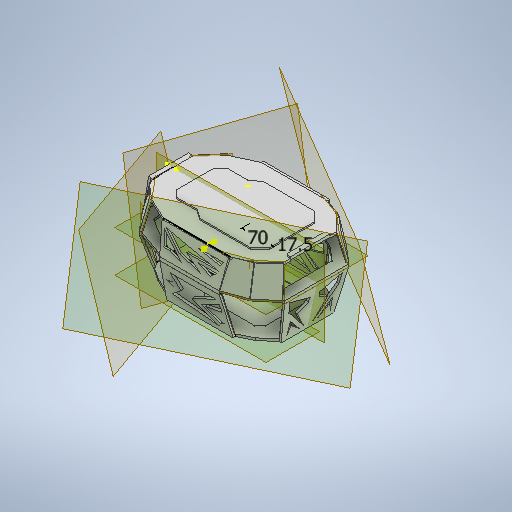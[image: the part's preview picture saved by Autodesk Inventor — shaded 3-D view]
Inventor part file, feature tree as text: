
AUTODESK INVENTOR PART (.ipt)
format: ipt  version: 2025.2 (Build 292293000, 293)  size: 6,096,896 bytes
history: native  units: mm
features: sketch x44, extrude x35, other x23, plane x17, loft x11, mirror x2, chamfer x2
ambient origin geometry x8: Origin, YZ Plane, XZ Plane, XY Plane, X Axis, Y Axis, Z Axis, Center Point
bodies: Body1 (feature_tree)
feature tree (134):
  extrude  "Extrusion2"  Depth=45.0mm
  extrude  "Extrusion3"  Depth=40.0mm
  plane  "Work Plane3"
  extrude  "Extrusion4"  Depth=145.0mm
  extrude  "Extrusion5"  Depth=55.0mm
  plane  "Work Plane4"
  extrude  "Extrusion6"  Depth=40.0mm
  sketch  "Sketch8"  dims[d17=165.0deg d18=15.0mm]
  sketch  "Sketch9"  dims[d20=10.0mm d21=40.0mm]
  sketch  "Sketch10"  dims[d22=5.0mm d23=5.0mm]
  loft  "Loft1"
  loft  "Loft2"
  extrude  "Extrusion7"  Depth=5.0mm
  extrude  "Extrusion8"  TaperAngle=90.0deg  [1 undecoded]
  extrude  "Extrusion9"  Depth=30.0mm
  sketch  "Sketch14"  dims[d30=45.0mm d31=20.0mm]
  sketch  "Sketch15"  dims[d32=45.0deg d39=5.0mm d40=0.0mm]
  sketch  "Sketch16"  dims[d41=3.0mm d42=3.0mm d43=0.0mm d44=0.0mm d45=150.0mm]
  loft  "Loft3"
  loft  "Loft4"
  loft  "Loft5"
  extrude  "Extrusion10"  Depth=3.0mm
  extrude  "Extrusion11"  Depth=10.0mm
  extrude  "Extrusion12"  Depth=10.0mm
  extrude  "Extrusion13"  Depth=10.0mm
  extrude  "Extrusion14"  Depth=10.0mm
  loft  "Loft7"
  loft  "Loft8"
  sketch  "Sketch22"  dims[d57=10.0mm d58=10.0mm]
  plane  "Work Plane5"
  extrude  "Extrusion15"  Depth=3.0mm TaperAngle=0.0deg
  plane  "Work Plane6"
  extrude  "Extrusion16"  Depth=10.0mm
  extrude  "Extrusion17"  Depth=50.0mm
  plane  "Work Plane7"
  extrude  "Extrusion18"  Depth=50.0mm
  sketch  "Sketch28"  dims[d71=27.925268mm d72=10.0mm]
  extrude  "Extrusion19"  Depth=10.0mm
  extrude  "Extrusion20"  Depth=60.0mm
  extrude  "Extrusion21"  Depth=5.0mm TaperAngle=0.0deg
  extrude  "Extrusion22"  TaperAngle=0.0deg  [1 undecoded]
  extrude  "Extrusion23"  TaperAngle=0.0deg  [1 undecoded]
  extrude  "Extrusion24"  Depth=4.0mm TaperAngle=0.0deg
  extrude  "Extrusion25"  TaperAngle=0.0deg  [1 undecoded]
  extrude  "Extrusion26"  TaperAngle=0.0deg  [1 undecoded]
  extrude  "Extrusion27"  TaperAngle=0.0deg  [1 undecoded]
  plane  "Work Plane8"
  mirror  "Mirror1"
  loft  "Loft9"
  loft  "Loft10"
  loft  "Loft11"
  loft  "Loft12"
  plane  "Work Plane14"
  plane  "Work Plane15"
  extrude  "Extrusion28"  TaperAngle=0.0deg  [1 undecoded]
  extrude  "Extrusion29"  Depth=4.0mm TaperAngle=0.0deg
  plane  "Work Plane16"
  extrude  "Extrusion30"  Depth=92.689mm
  mirror  "Mirror2"
  extrude  "Extrusion31"  Depth=70.0mm
  sketch  "Sketch42"  dims[d126=4.0mm d127=0.0mm d128=4.0mm d129=0.0mm]
  extrude  "Extrusion32"  Depth=5.0mm
  extrude  "Extrusion33"  Depth=70.0mm
  extrude  "Extrusion34"  Depth=2.0mm
  extrude  "Extrusion35"  TaperAngle=90.0deg  [1 undecoded]
  chamfer  "Chamfer1"  Distance=23.0mm
  extrude  "Extrusion36"  Depth=70.0mm
  chamfer  "Chamfer2"  Distance=3.0mm
  sketch  "Sketch1"  dims[d6=115.0mm d8=45.0mm]
  other  "Image1"
  sketch  "Sketch3"  dims[d9=45.0deg d10=40.0mm]
  sketch  "Sketch4"  dims[d11=27.925268mm d12=145.0mm]
  sketch  "Sketch5"  dims[d13=27.052603mm d14=55.0mm]
  sketch  "Sketch6"  dims[d15=27.052603mm d16=40.0mm]
  other  "Edges1"
  other  "Edges2"
  other  "Edges3"
  other  "Edges4"
  sketch  "Sketch11"  dims[d24=40.0mm d25=90.0deg]
  sketch  "Sketch12"  dims[d26=30.0mm d27=110.0mm]
  sketch  "Sketch13"  dims[d28=25.0mm d29=25.307274mm]
  other  "Edges5"
  other  "Edges6"
  other  "Edges7"
  other  "Edges8"
  other  "Edges9"
  other  "Edges10"
  sketch  "Sketch17"  dims[d46=10.0mm d48=10.0mm]
  sketch  "Sketch18"  dims[d49=10.0mm d50=22.68928mm]
  sketch  "Sketch19"  dims[d51=10.0mm d52=10.0mm]
  sketch  "Sketch20"  dims[d53=10.0mm d54=10.0mm]
  sketch  "Sketch21"  dims[d55=10.0mm d56=10.0mm]
  other  "Edges13"
  other  "Edges14"
  other  "Edges15"
  other  "Edges16"
  sketch  "Sketch23"  dims[d59=5.0mm d60=0.0mm d61=3.0mm d62=3.0mm d63=0.0mm d64=0.0mm]
  sketch  "Sketch24"  dims[d65=-90.0mm d66=10.0mm]
  sketch  "Sketch25"  dims[d67=70.0mm d68=50.0mm]
  sketch  "Sketch26"  dims[d69=22.68928mm d70=50.0mm]
  sketch  "Sketch29"  dims[d73=50.0mm d74=60.0mm]
  sketch  "Sketch30"  dims[d75=70.0mm d76=5.0mm d77=0.0mm]
  sketch  "Sketch31"  dims[d78=0.0mm d79=90.0deg d80=0.0mm d81=90.0deg]
  sketch  "Sketch32"  dims[d82=0.0mm d83=90.0deg d84=0.0mm d85=90.0deg]
  sketch  "Sketch33"  dims[d86=4.0mm d87=0.0mm d88=4.0mm d89=0.0mm]
  sketch  "Sketch34"  dims[d90=4.0mm d91=0.0mm d92=0.0mm d93=90.0deg]
  sketch  "Sketch35"  dims[d94=0.0mm d95=90.0deg d96=0.0mm d97=90.0deg]
  sketch  "Sketch36"  dims[d98=0.0mm d99=90.0deg d100=0.0mm d101=90.0deg]
  sketch  "Sketch37"  dims[d102=0.0mm d103=90.0deg d104=4.0mm d105=0.0mm]
  plane  "Work Plane9"
  plane  "Work Plane10"
  plane  "Work Plane11"
  plane  "Work Plane12"
  plane  "Work Plane13"
  other  "Edges17"
  other  "Edges18"
  other  "Edges19"
  other  "Edges20"
  other  "Edges21"
  other  "Edges22"
  other  "Edges23"
  other  "Edges24"
  sketch  "Sketch38"  dims[d106=4.0mm d107=0.0mm d108=4.0mm d109=0.0mm]
  sketch  "Sketch39"  dims[d110=4.0mm d111=0.0mm d112=4.0mm d113=0.0mm]
  sketch  "Sketch40"  dims[d118=0.0mm d119=90.0deg d120=0.0mm d121=90.0deg]
  plane  "Work Plane17"
  plane  "Work Plane18"
  plane  "Work Plane19"
  sketch  "Sketch41"  dims[d122=0.0mm d123=90.0deg d124=0.0mm d125=90.0deg]
  sketch  "Sketch43"  dims[d130=4.0mm d131=0.0mm d132=92.689mm]
  sketch  "Sketch44"  dims[d133=4.0mm d134=0.0mm d135=70.0mm]
  sketch  "Sketch45"  dims[d136=17.5mm d137=5.0mm]
  sketch  "Sketch46"  dims[d138=25.0mm d139=70.0mm]
  sketch  "Sketch47"  dims[d140=25.0mm d141=17.5mm d142=90.0deg d143=23.0mm d144=0.0mm d145=70.0mm d146=3.0mm d147=17.5mm d148=0.0mm d149=25.0mm d150=30.0mm d151=15.0deg d152=90.0deg d153=5.0mm d154=20.0mm d155=90.0deg d156=4.363323mm d157=17.5mm d158=0.0mm d159=25.0mm d160=165.0deg d161=40.0mm d162=150.0deg d163=50.0mm d164=1.745329mm d165=40.0mm d166=5.0mm d167=40.0mm d168=30.543262mm d169=17.5mm d170=0.0mm d171=10.0mm d172=100.0mm d173=150.0deg d174=40.0mm d175=19.198622mm d176=100.0mm d177=70.0mm d178=30.0deg d179=100.0mm d180=10.0mm d181=10.0mm d182=10.0mm d183=4.363323mm d184=40.0mm d185=40.0mm d186=6.981317mm d187=20.0mm d188=24.43461mm d189=16.0mm d190=10.0mm d191=0.0mm d192=80.0mm d193=24.43461mm d194=120.0mm d195=30.0deg d196=40.0mm d197=30.0deg d198=50.0mm d199=10.0mm d200=50.0mm d201=55.0mm d202=1.745329mm d203=30.0mm d204=27.925268mm d205=40.0mm d206=5.0mm d207=30.0mm d208=30.0mm d209=17.453293mm d210=60.0mm d211=30.0mm d212=50.0mm d213=0.0mm d214=10.0mm d215=10.0mm d216=10.0mm d217=10.0mm d218=90.0deg d219=10.0mm d220=20.0mm d221=10.0mm d222=17.453293mm d223=25.0mm d224=22.68928mm d225=70.0mm d226=10.0mm d227=40.0mm d228=22.68928mm d229=20.0mm d230=75.0deg d231=50.0mm d232=0.0mm d233=5.0mm d234=0.0mm d235=5.0mm d236=0.0mm d238=0.0mm d239=90.0deg d240=0.0mm d241=90.0deg d242=0.0mm d243=90.0deg d244=0.0mm d245=90.0deg d246=0.0mm d247=90.0deg d248=0.0mm d249=90.0deg d250=0.0mm d251=90.0deg d252=0.0mm d253=90.0deg d254=3.0mm d255=0.0mm d256=3.0mm d257=0.0mm d258=3.0mm d259=0.0mm d260=30.0mm d261=50.0mm d262=90.0mm d263=30.0mm d264=5.0mm d265=0.0mm d266=20.0mm d267=100.0mm d268=20.0mm d269=100.0mm d270=30.0mm d271=40.0mm d272=30.0mm d273=5.0mm d274=5.0mm d275=0.0mm d276=0.0mm d277=10.0mm d278=10.0mm d279=30.0mm d280=0.0mm d281=20.0mm d282=20.0mm d283=20.0mm d284=90.0deg d285=10.0mm d286=0.0mm d287=20.0mm d288=100.0mm d289=0.0mm d290=10.0mm d291=10.0mm d292=10.0mm d293=0.0mm d294=6.0mm d295=2.0mm d296=45.0deg d297=20.0mm d298=13.0mm d299=20.0mm d300=13.0mm d301=20.0mm d302=13.0mm d303=20.0mm d304=13.0mm d305=20.0mm d306=0.0mm d307=20.0mm d308=2.0mm d309=45.0deg]
note: 8 required parameter values undecoded (feature->parameter linkage not recoverable at this tier; creation-order binding heuristic only, values carry confidence <= 0.55)
